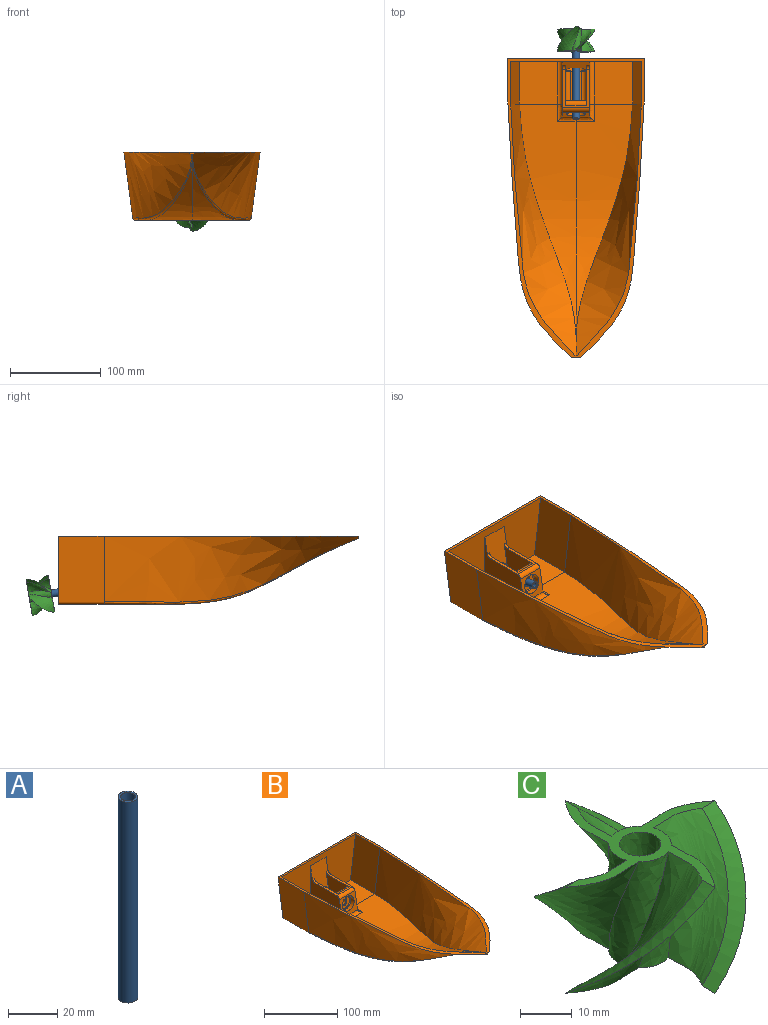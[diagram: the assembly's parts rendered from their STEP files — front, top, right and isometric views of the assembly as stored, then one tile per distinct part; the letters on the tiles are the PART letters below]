
ASSEMBLY  parts=3 mates=2
PART A: 4 faces, bbox 8x8x100 mm
  f0: cylinder r=3mm len=100mm, axis (0,0,-1), area 1885mm2, adj f2,f3
  f1: cylinder r=4mm len=100mm, axis (0,0,-1), area 2513.3mm2, adj f2,f3
  f2: plane 8x8mm, normal (0,0,1), area 22mm2, adj f0,f1
  f3: plane 8x8mm, normal (0,0,-1), area 22mm2, adj f0,f1
PART B: 57 faces, bbox 156x377x83.2 mm
  f0: plane 62.35x30.37mm, normal (0,-0.98,0.17), area 1200.4mm2, adj f1,f7,f29,f30,f38,f43,f44,f51
  f1: plane 32.14x13mm, normal (0,0,1), area 417.9mm2, adj f0,f2,f52,f54
  f2: plane 32.9x23.32mm, normal (0,1,0), area 681.1mm2, adj f1,f35,f43,f44,f52,f54,f55
  f3: plane 46.99x42.37mm, normal (0,0,1), area 1991.3mm2, adj f5,f7,f25,f26,f47
  f4: plane 46.99x42.37mm, normal (0,0,1), area 1991.3mm2, adj f6,f7,f27,f28,f45
  f5: offset ~286x80.23mm, area 8421.4mm2, adj f3,f6,f25,f49,f50
  f6: offset ~286x80.23mm, area 8421.4mm2, adj f4,f5,f27,f46,f48
  f7: plane 143.95x72mm, normal (0,-1,0), area 7802.9mm2, adj f0,f3,f4,f8,f26,f28,f29,f30
  f8: plane 330x150mm, normal (0,0,1), area 3125.1mm2, adj f7,f9,f11,f13,f14,f16,f17,f24
  f9: plane 10.03x2.97mm, normal (0,-1,0), area 15.5mm2, adj f8,f11,f16,f20,f22
  f10: bspline ~280x74.23mm, area 6005.9mm2, adj f12,f15,f19
  f11: bspline ~280x77.23mm, area 18326mm2, adj f8,f9,f13,f19,f20
  f12: plane 124.75x50mm, normal (0,0,-1), area 6237.3mm2, adj f10,f14,f15,f18,f19,f21,f23
  f13: plane 72.4x50mm, normal (0.99,0,-0.13), area 3651.9mm2, adj f8,f11,f14,f18,f19
  f14: plane 150.32x75.32mm, normal (0,1,0), area 10439.6mm2, adj f8,f12,f13,f17,f18,f21,f36
  f15: bspline ~280x74.23mm, area 6005.9mm2, adj f10,f12,f23
  f16: bspline ~280x77.23mm, area 18326mm2, adj f8,f9,f17,f22,f23
  f17: plane 72.4x50mm, normal (-0.99,0,-0.13), area 3651.9mm2, adj f8,f14,f16,f21,f23
  f18: cylinder r=3mm len=50mm, axis (0,-1,0), area 215.7mm2, adj f12,f13,f14,f19
  f19: bspline ~267.24x66.06mm, area 841.5mm2, adj f10,f11,f12,f13,f18,f20
  f20: bspline ~29.24x12.4mm, area 25.6mm2, adj f9,f11,f19,f22
  f21: cylinder r=3mm len=50mm, axis (0,-1,0), area 215.7mm2, adj f12,f14,f17,f23
  f22: bspline ~29.24x12.4mm, area 25.6mm2, adj f9,f16,f20,f23
  f23: bspline ~267.24x66.06mm, area 841.5mm2, adj f12,f15,f16,f17,f21,f22
  f24: plane 2.44x0.68mm, normal (0,1,0), area 0.8mm2, adj f8,f25,f27
  f25: offset ~286x83.23mm, area 17583.4mm2, adj f3,f5,f8,f24,f26,f27
  f26: plane 72x46.96mm, normal (-0.99,0,0.13), area 3408.6mm2, adj f3,f7,f8,f25
  f27: offset ~286x83.23mm, area 17583.4mm2, adj f4,f6,f8,f24,f25,f28
  f28: plane 72x46.96mm, normal (0.99,0,0.13), area 3408.6mm2, adj f4,f7,f8,f27
  f29: plane 60.81x56.98mm, normal (1,0,0), area 1940.2mm2, adj f0,f7,f31,f32,f47,f49,f53,f56
  f30: plane 60.81x56.98mm, normal (-1,0,0), area 1940.2mm2, adj f0,f7,f31,f32,f45,f46,f51,f56
  f31: plane 30.16x29.27mm, normal (0,-0.98,0.17), area 511.2mm2, adj f29,f30,f33,f46,f48,f49,f50,f56
  f32: plane 42.38x30mm, normal (0,0,1), area 361.2mm2, adj f29,f30,f43,f44,f51,f53,f55,f56
  f33: cylinder r=11mm len=22.88mm, axis (0,-0.98,0.17), area 483.8mm2, adj f31,f40
  f34: plane 20x19.7mm, normal (0,-0.98,0.17), area 227.6mm2, adj f39,f40
  f35: cylinder r=4.25mm len=9.58mm, axis (0,-0.98,0.17), area 165.6mm2, adj f2,f39
  f36: cylinder r=4.25mm len=9.02mm, axis (0,-0.98,0.17), area 79.7mm2, adj f14,f42
  f37: plane 20x19.7mm, normal (0,-0.98,0.17), area 227.6mm2, adj f41,f42
  f38: cylinder r=11mm len=22.88mm, axis (0,-0.98,0.17), area 483.8mm2, adj f0,f41
  f39: cone r=4.25mm half-angle=45deg, axis (0,-0.98,0.17), area 42.2mm2, adj f34,f35
  f40: cone r=10mm half-angle=45deg, axis (0,-0.98,0.17), area 93.3mm2, adj f33,f34
  f41: cone r=10mm half-angle=45deg, axis (0,-0.98,0.17), area 93.3mm2, adj f37,f38
  f42: cone r=4.25mm half-angle=45deg, axis (0,-0.98,0.17), area 42.2mm2, adj f36,f37
  f43: plane 44.5x36.72mm, normal (-1,0,0), area 1178.6mm2, adj f0,f2,f32,f53,f54,f55
  f44: plane 44.5x36.72mm, normal (1,0,0), area 1178.6mm2, adj f0,f2,f32,f51,f52,f55
  f45: cylinder r=5mm len=46.99mm, axis (0,1,0), area 369.1mm2, adj f4,f7,f30,f46
  f46: bspline ~127.29x5.43mm, area 123.4mm2, adj f6,f30,f31,f45,f48
  f47: cylinder r=5mm len=46.99mm, axis (0,-1,0), area 369.1mm2, adj f3,f7,f29,f49
  f48: bspline ~39.58x4.94mm, area 122.6mm2, adj f6,f31,f46,f50
  f49: bspline ~127.29x5.43mm, area 123.4mm2, adj f5,f29,f31,f47,f50
  f50: bspline ~31.1x4.94mm, area 122.6mm2, adj f5,f31,f48,f49
  f51: cylinder r=5mm len=4.92mm, axis (1,0,0), area 24.4mm2, adj f0,f30,f32,f44
  f52: cylinder r=5mm len=33.03mm, axis (0,1,0), area 255.9mm2, adj f0,f1,f2,f44
  f53: cylinder r=5mm len=4.92mm, axis (1,0,0), area 24.4mm2, adj f0,f29,f32,f43
  f54: cylinder r=5mm len=33.03mm, axis (0,-1,0), area 255.9mm2, adj f0,f1,f2,f43
  f55: cylinder r=5mm len=23mm, axis (-1,0,0), area 180.6mm2, adj f2,f32,f43,f44
  f56: cylinder r=5mm len=30mm, axis (-1,0,0), area 209.4mm2, adj f29,f30,f31,f32
PART C: 19 faces, bbox 40.9x40.9x25 mm
  f0: bspline ~25x20.67mm, area 177.3mm2, adj f4,f5,f15,f18
  f1: bspline ~25x21.71mm, area 177.3mm2, adj f4,f5,f12,f14
  f2: bspline ~25x21.71mm, area 177.3mm2, adj f4,f5,f7,f11
  f3: bspline ~25x18.1mm, area 629.1mm2, adj f4,f5
  f4: plane 40.86x40.86mm, normal (0,0,-1), area 177.9mm2, adj f0,f1,f2,f3,f6,f7,f8,f9
  f5: plane 40.86x40.86mm, normal (0,0,1), area 177.9mm2, adj f0,f1,f2,f3,f6,f7,f8,f9
  f6: bspline ~25x20.43mm, area 132.3mm2, adj f4,f5,f7,f9
  f7: bspline ~25.51x25mm, area 525.4mm2, adj f2,f4,f5,f6
  f8: bspline ~25x20.67mm, area 177.3mm2, adj f4,f5,f9,f17
  f9: bspline ~25x19.23mm, area 358.1mm2, adj f4,f5,f6,f8
  f10: bspline ~25x20.43mm, area 132.3mm2, adj f4,f5,f11,f12
  f11: bspline ~25x19.23mm, area 358.1mm2, adj f2,f4,f5,f10
  f12: bspline ~25.51x25mm, area 525.4mm2, adj f1,f4,f5,f10
  f13: bspline ~25x20.43mm, area 132.3mm2, adj f4,f5,f14,f15
  f14: bspline ~25x19.23mm, area 358.1mm2, adj f1,f4,f5,f13
  f15: bspline ~25.51x25mm, area 525.4mm2, adj f0,f4,f5,f13
  f16: bspline ~25x20.43mm, area 132.3mm2, adj f4,f5,f17,f18
  f17: bspline ~25.51x25mm, area 525.4mm2, adj f4,f5,f8,f16
  f18: bspline ~25x19.23mm, area 358.1mm2, adj f0,f4,f5,f16
PLACE A rot(axis=(-1,0,0),100deg) t=(-35.29,-11.4,76.61)mm
PLACE B t=(21.17,-2.01,14.71)mm
PLACE C rot(axis=(-1,0,0),100deg) t=(21.17,55.88,26.28)mm
MATE fastened C.f5 <-> A.f0  axis (0,0.98,-0.17) through (21.17,80.5,21.94)mm
MATE revolute A.f0 <-> B.f41  axis (0,-0.98,0.17) through (21.17,-17.98,39.31)mm
